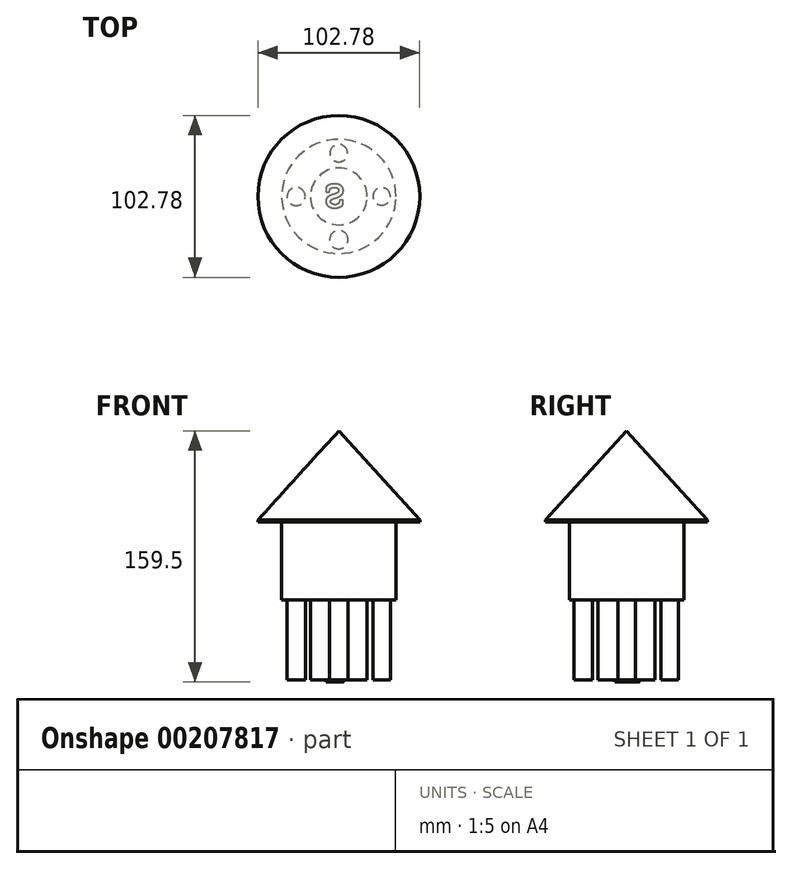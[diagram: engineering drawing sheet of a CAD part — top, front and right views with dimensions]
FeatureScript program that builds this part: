
annotation { "Feature Type Name" : "Feature", "Feature Type Description" : "" }
export const myFeature = defineFeature(function(context is Context, id is Id, definition is map)
    precondition{}
    {
        {
            var Q0;
            Q0=qCreatedBy(makeId("Right.planeOp"),FACE);
            var sketch = newSketch(context, id + "F0", { "sketchPlane" : qUnion([Q0])});
            skLineSegment(sketch, "E0", {"start": v(0, 0) * mm, "end": v(0, 56.63) * mm});
            skLineSegment(sketch, "E1", {"start": v(0, 56.63) * mm, "end": v(51.4, 0) * mm});
            skLineSegment(sketch, "E2", {"start": v(0, 0) * mm, "end": v(51.4, 0) * mm});
            skSolve(sketch);
        }
        {
            var Q0;
            Q0=makeQuery(id+"F0.imprint","IMPRINT",FACE,{"disambiguationData":[TD([[makeQuery(id+"F0.imprint","IMPRINT",EDGE,{"derivedFrom":sQuery(id+"F0.wireOp",EDGE,"E0")}),-1.0]])]});
            var Q1;
            Q1=sQuery(id+"F0.wireOp",EDGE,"E0");
            revolve(context, id + "F1", {"entities" : qUnion([Q0]), "axis" : qUnion([Q1]), "revolveType" : RevolveType.FULL});
        }
        {
            var Q0;
            Q0=makeQuery(id+"F1.opRevolve","SWEPT_FACE",FACE,{"disambiguationData":[OSD([sQuery(id+"F0.wireOp",EDGE,"E2")])]});
            var sketch = newSketch(context, id + "F2", { "sketchPlane" : qUnion([Q0])});
            skCircle(sketch, "E3", {"center": v(0, 0) * mm, "radius": 36.29 * mm});
            skSolve(sketch);
        }
        {
            var Q0;
            Q0 = qSketchRegion(id + "F2", true);
            var Q1;
            Q1=makeQuery(id+"F2.imprint","IMPRINT",FACE,{"disambiguationData":[TD([[makeQuery(id+"F2.imprint","IMPRINT",EDGE,{"derivedFrom":sQuery(id+"F2.wireOp",EDGE,"E3")}),1.0]])]});
            extrude(context, id + "F3", {"entities" : qUnion([Q0, Q1]), "operationType" : NewBodyOperationType.ADD, "depth" : 50.8 * mm});
        }
        {
            var Q0;
            Q0=makeQuery(id+"F3.opExtrude","CAP_FACE",FACE,{"disambiguationData":[OSD([sQuery(id+"F2.wireOp",EDGE,"E3")])],"isStart":false});
            var sketch = newSketch(context, id + "F4", { "sketchPlane" : qUnion([Q0])});
            skCircle(sketch, "E4", {"center": v(0, 0) * mm, "radius": 18.04 * mm});
            skSolve(sketch);
        }
        {
            var Q0;
            Q0=makeQuery(id+"F4.imprint","IMPRINT",FACE,{"disambiguationData":[TD([[makeQuery(id+"F4.imprint","IMPRINT",EDGE,{"derivedFrom":sQuery(id+"F4.wireOp",EDGE,"E4")}),1.0]])]});
            extrude(context, id + "F5", {"entities" : qUnion([Q0]), "operationType" : NewBodyOperationType.ADD, "depth" : 50.8 * mm});
        }
        {
            var Q0;
            Q0=makeQuery(id+"F5.opExtrude","CAP_FACE",FACE,{"disambiguationData":[OSD([sQuery(id+"F4.wireOp",EDGE,"E4")])],"isStart":false});
            var sketch = newSketch(context, id + "F6", { "sketchPlane" : qUnion([Q0])});
            skText(sketch, "E5", { "text": "S", "fontName": "RobotoSlab-Bold.ttf"});
            const initialGuessF6  = {"E5": [-0.00925, -0.00776, 1, 0, 0.0151]};
            skSetInitialGuess(sketch, initialGuessF6);
            skSolve(sketch);
        }
        {
            var Q0;
            Q0 = qSketchRegion(id + "F6", true);
            extrude(context, id + "F7", {"entities" : qUnion([Q0]), "operationType" : NewBodyOperationType.ADD, "depth" : 0.25 * mm});
        }
        {
            var Q0;
            Q0=makeQuery(id+"F6.imprint","IMPRINT",FACE,{"disambiguationData":[TD([[makeQuery(id+"F6.imprint","IMPRINT",EDGE,{"derivedFrom":sQuery(id+"F6.wireOp",EDGE,"E5.sketch_text.stroke-0")}),-1.0]])]});
            var Q1;
            Q1=makeQuery(id+"F1.opRevolve","SWEPT_FACE",FACE,{"disambiguationData":[OSD([sQuery(id+"F0.wireOp",EDGE,"E2")])]});
            extrude(context, id + "F8", {"entities" : qUnion([Q0, Q1]), "operationType" : NewBodyOperationType.ADD, "depth" : 1.27 * mm});
        }
        {
            var Q0;
            Q0=makeQuery(id+"F3.opExtrude","CAP_FACE",FACE,{"disambiguationData":[OSD([sQuery(id+"F2.wireOp",EDGE,"E3")])],"isStart":false});
            var sketch = newSketch(context, id + "F9", { "sketchPlane" : qUnion([Q0])});
            skCircle(sketch, "E6", {"center": v(27.25, 0) * mm, "radius": 5.53 * mm});
            skCircle(sketch, "E7", {"center": v(0, -27.5) * mm, "radius": 5.55 * mm});
            skCircle(sketch, "E8", {"center": v(-27.04, 0) * mm, "radius": 5.76 * mm});
            skCircle(sketch, "E9", {"center": v(0, 27.5) * mm, "radius": 5.84 * mm});
            skSolve(sketch);
        }
        {
            var Q0;
            Q0=makeQuery(id+"F9.imprint","IMPRINT",FACE,{"disambiguationData":[TD([[makeQuery(id+"F9.imprint","IMPRINT",EDGE,{"derivedFrom":sQuery(id+"F9.wireOp",EDGE,"E6")}),1.0]])]});
            var Q1;
            Q1=makeQuery(id+"F9.imprint","IMPRINT",FACE,{"disambiguationData":[TD([[makeQuery(id+"F9.imprint","IMPRINT",EDGE,{"derivedFrom":sQuery(id+"F9.wireOp",EDGE,"E7")}),1.0]])]});
            var Q2;
            Q2=makeQuery(id+"F9.imprint","IMPRINT",FACE,{"disambiguationData":[TD([[makeQuery(id+"F9.imprint","IMPRINT",EDGE,{"derivedFrom":sQuery(id+"F9.wireOp",EDGE,"E9")}),1.0]])]});
            var Q3;
            Q3=makeQuery(id+"F9.imprint","IMPRINT",FACE,{"disambiguationData":[TD([[makeQuery(id+"F9.imprint","IMPRINT",EDGE,{"derivedFrom":sQuery(id+"F9.wireOp",EDGE,"E8")}),1.0]])]});
            var Q4;
            Q4=sQuery(id+"F9.wireOp",EDGE,"E6");
            extrude(context, id + "F10", {"entities" : qUnion([Q0, Q1, Q2, Q3]), "operationType" : NewBodyOperationType.ADD, "surfaceEntities" : qUnion([Q4]), "depth" : 25.4 * mm});
        }
        {
            var Q0;
            Q0=makeQuery(id+"F10.opExtrude","CAP_FACE",FACE,{"disambiguationData":[OSD([sQuery(id+"F9.wireOp",EDGE,"E9")])],"isStart":false});
            var Q1;
            Q1=makeQuery(id+"F10.opExtrude","CAP_FACE",FACE,{"disambiguationData":[OSD([sQuery(id+"F9.wireOp",EDGE,"E6")])],"isStart":false});
            var Q2;
            Q2=makeQuery(id+"F10.opExtrude","CAP_FACE",FACE,{"disambiguationData":[OSD([sQuery(id+"F9.wireOp",EDGE,"E7")])],"isStart":false});
            var Q3;
            Q3=makeQuery(id+"F10.opExtrude","CAP_FACE",FACE,{"disambiguationData":[OSD([sQuery(id+"F9.wireOp",EDGE,"E8")])],"isStart":false});
            extrude(context, id + "F11", {"entities" : qUnion([Q0, Q1, Q2, Q3]), "operationType" : NewBodyOperationType.ADD, "depth" : 25.4 * mm});
        }
    });
